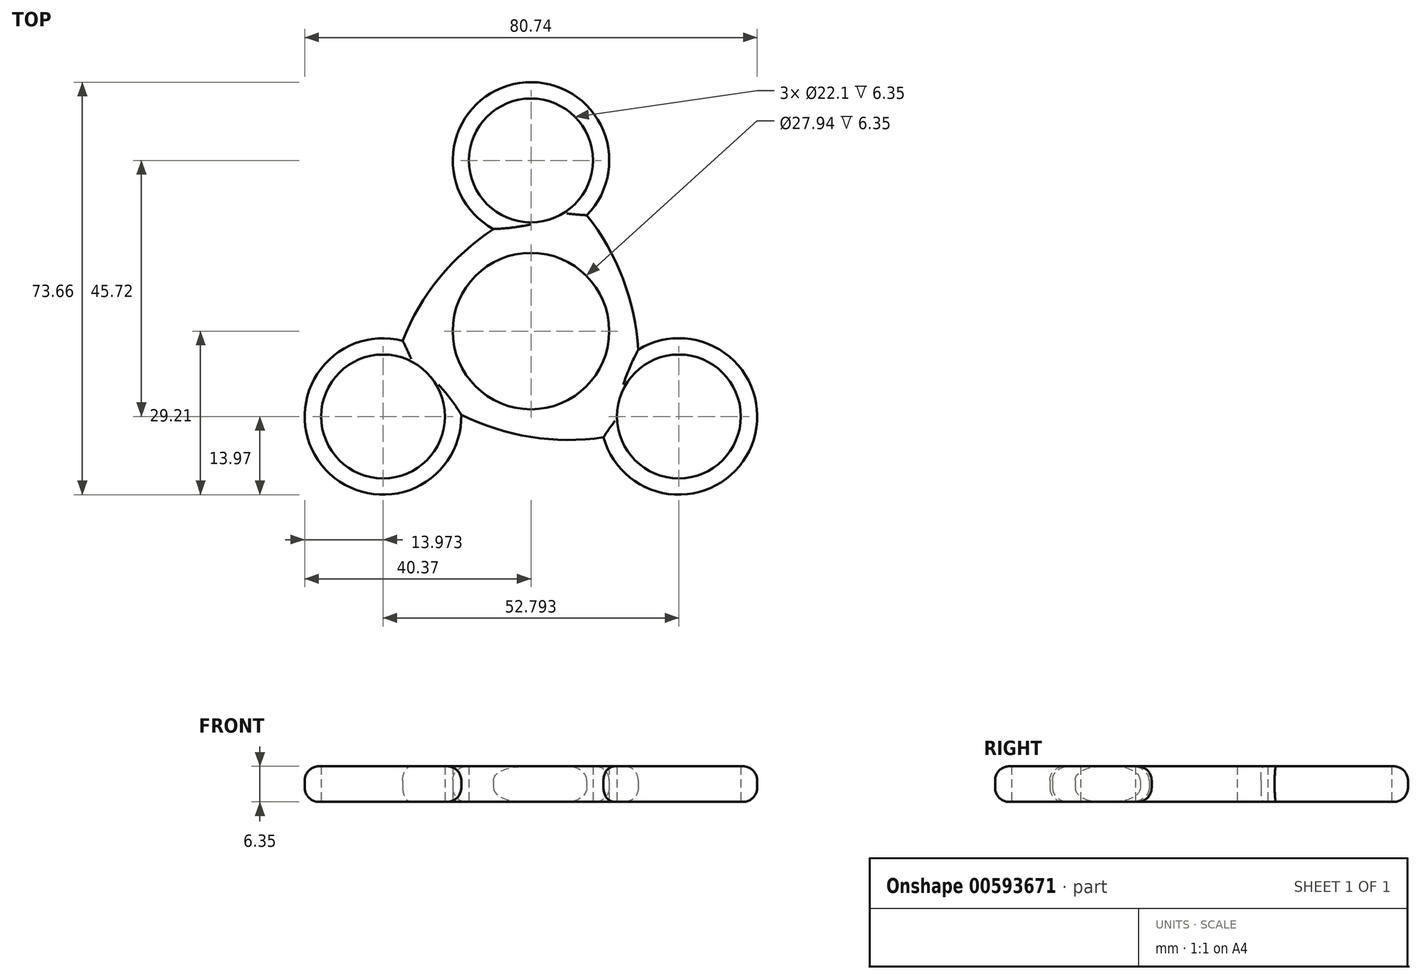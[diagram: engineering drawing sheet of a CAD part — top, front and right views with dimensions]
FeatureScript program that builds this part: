
annotation { "Feature Type Name" : "Feature", "Feature Type Description" : "" }
export const myFeature = defineFeature(function(context is Context, id is Id, definition is map)
    precondition{}
    {
        {
            var Q0;
            Q0=qCreatedBy(makeId("Top.planeOp"),FACE);
            var sketch = newSketch(context, id + "F0", { "sketchPlane" : qUnion([Q0])});
            skCircle(sketch, "E0", {"center": v(0, 0) * mm, "radius": 11.05 * mm});
            skCircle(sketch, "E1", {"center": v(0, 0) * mm, "radius": 13.97 * mm});
            skCircle(sketch, "E2", {"center": v(0, 30.48) * mm, "radius": 11.05 * mm});
            skCircle(sketch, "E3", {"center": v(0, 30.48) * mm, "radius": 13.97 * mm});
            skCircle(sketch, "E4.1.0", {"center": v(-26.4, -15.24) * mm, "radius": 11.05 * mm});
            skCircle(sketch, "E4.1.1", {"center": v(-26.4, -15.24) * mm, "radius": 13.97 * mm});
            skCircle(sketch, "E4.2.0", {"center": v(26.4, -15.24) * mm, "radius": 11.05 * mm});
            skCircle(sketch, "E4.2.1", {"center": v(26.4, -15.24) * mm, "radius": 13.97 * mm});
            skArc(sketch, "E5", {"start": v(-6.7, 18.22) * mm, "mid": v(-16.34, 9.5) * mm, "end": v(-22.9, -1.72) * mm});
            skArc(sketch, "E6.1.0", {"start": v(-12.43, -14.92) * mm, "mid": v(-0.06, -18.9) * mm, "end": v(12.93, -18.97) * mm});
            skArc(sketch, "E6.2.0", {"start": v(19.13, -3.3) * mm, "mid": v(16.4, 9.4) * mm, "end": v(9.96, 20.68) * mm});
            skSolve(sketch);
        }
        {
            var Q0;
            Q0=makeQuery(id+"F0.imprint","IMPRINT",FACE,{"disambiguationData":[TD([[makeQuery(id+"F0.imprint","IMPRINT",EDGE,{"derivedFrom":sQuery(id+"F0.wireOp",EDGE,"E2")}),-1.0]])]});
            var Q1;
            Q1=makeQuery(id+"F0.imprint","IMPRINT",FACE,{"disambiguationData":[TD([[makeQuery(id+"F0.imprint","IMPRINT",EDGE,{"derivedFrom":sQuery(id+"F0.wireOp",EDGE,"E1")}),-1.0]])]});
            var Q2;
            Q2=makeQuery(id+"F0.imprint","IMPRINT",FACE,{"disambiguationData":[TD([[makeQuery(id+"F0.imprint","IMPRINT",EDGE,{"derivedFrom":sQuery(id+"F0.wireOp",EDGE,"E4.2.0")}),-1.0]])]});
            var Q3;
            Q3=makeQuery(id+"F0.imprint","IMPRINT",FACE,{"disambiguationData":[TD([[makeQuery(id+"F0.imprint","IMPRINT",EDGE,{"derivedFrom":sQuery(id+"F0.wireOp",EDGE,"E4.1.0")}),-1.0]])]});
            extrude(context, id + "F1", {"entities" : qUnion([Q0, Q1, Q2, Q3]), "depth" : 6.35 * mm, "offsetDistance" : 25.4 * mm});
        }
        {
            var Q0;
            Q0=makeQuery(id+"F1.opExtrude","CAP_EDGE",EDGE,{"disambiguationData":[OSD([sQuery(id+"F0.wireOp",EDGE,"E4.1.1")])],"isStart":false});
            var Q1;
            Q1=makeQuery(id+"F1.opExtrude","CAP_EDGE",EDGE,{"disambiguationData":[OSD([sQuery(id+"F0.wireOp",EDGE,"E5")])],"isStart":false});
            var Q2;
            Q2=makeQuery(id+"F1.opExtrude","CAP_EDGE",EDGE,{"disambiguationData":[OSD([sQuery(id+"F0.wireOp",EDGE,"E3")])],"isStart":false});
            var Q3;
            Q3=makeQuery(id+"F1.opExtrude","CAP_EDGE",EDGE,{"disambiguationData":[OSD([sQuery(id+"F0.wireOp",EDGE,"E6.2.0")])],"isStart":false});
            var Q4;
            Q4=makeQuery(id+"F1.opExtrude","CAP_EDGE",EDGE,{"disambiguationData":[OSD([sQuery(id+"F0.wireOp",EDGE,"E4.2.1")])],"isStart":false});
            var Q5;
            Q5=makeQuery(id+"F1.opExtrude","CAP_EDGE",EDGE,{"disambiguationData":[OSD([sQuery(id+"F0.wireOp",EDGE,"E6.1.0")])],"isStart":false});
            fillet(context, id + "F2", {"entities" : qUnion([Q0, Q1, Q2, Q3, Q4, Q5]), "radius" : 2.54 * mm, "tangentPropagation" : true, "allowEdgeOverflow" : false});
        }
        {
            var Q0;
            Q0=makeQuery(id+"F1.opExtrude","CAP_EDGE",EDGE,{"disambiguationData":[OSD([sQuery(id+"F0.wireOp",EDGE,"E4.1.1")])],"isStart":true});
            var Q1;
            Q1=makeQuery(id+"F1.opExtrude","CAP_EDGE",EDGE,{"disambiguationData":[OSD([sQuery(id+"F0.wireOp",EDGE,"E5")])],"isStart":true});
            var Q2;
            Q2=makeQuery(id+"F1.opExtrude","CAP_EDGE",EDGE,{"disambiguationData":[OSD([sQuery(id+"F0.wireOp",EDGE,"E6.1.0")])],"isStart":true});
            var Q3;
            Q3=makeQuery(id+"F1.opExtrude","CAP_EDGE",EDGE,{"disambiguationData":[OSD([sQuery(id+"F0.wireOp",EDGE,"E4.2.1")])],"isStart":true});
            var Q4;
            Q4=makeQuery(id+"F1.opExtrude","CAP_EDGE",EDGE,{"disambiguationData":[OSD([sQuery(id+"F0.wireOp",EDGE,"E6.2.0")])],"isStart":true});
            var Q5;
            Q5=makeQuery(id+"F1.opExtrude","CAP_EDGE",EDGE,{"disambiguationData":[OSD([sQuery(id+"F0.wireOp",EDGE,"E3")])],"isStart":true});
            fillet(context, id + "F3", {"entities" : qUnion([Q0, Q1, Q2, Q3, Q4, Q5]), "radius" : 2.54 * mm, "tangentPropagation" : true, "allowEdgeOverflow" : false});
        }
    });
